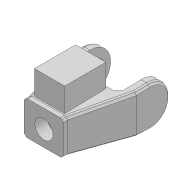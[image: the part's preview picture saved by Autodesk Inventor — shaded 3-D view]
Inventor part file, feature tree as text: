
AUTODESK INVENTOR PART (.ipt)
format: ipt  version: 2018 (Build 220112000, 112)  size: 759,296 bytes
history: native  units: mm
features: sketch x38, extrude x36, projected_geometry x30, chamfer x9, fillet x6, hole x3, mirror x2, plane x1
ambient origin geometry x8: Origin, YZ Plane, XZ Plane, XY Plane, X Axis, Y Axis, Z Axis, Center Point
bodies: Solid1 (feature_tree)
feature tree (125):
  extrude  "Extrusion1"  Depth=45.0mm
  extrude  "Extrusion2"  Depth=2.25mm
  hole  "Hole1"  [1 undecoded]
  hole  "Hole2"  [1 undecoded]
  fillet  "Fillet1"  Radius=14.0mm
  extrude  "Extrusion3"  Depth=18.5mm
  extrude  "Extrusion4"  Depth=10.0mm
  extrude  "Extrusion5"  Depth=2.0mm
  extrude  "Extrusion6"  Depth=2.0mm
  hole  "Hole3"  [1 undecoded]
  extrude  "Extrusion7"  Depth=2.0mm
  extrude  "Extrusion8"  Depth=5.0mm TaperAngle=0.0deg
  extrude  "Extrusion9"  Depth=10.0mm
  extrude  "Extrusion10"  Depth=10.0mm
  extrude  "Extrusion11"  Depth=14.5mm
  extrude  "Extrusion12"  Depth=14.5mm
  extrude  "Extrusion13"  Depth=5.0mm
  extrude  "Extrusion14"  Depth=2.25mm
  extrude  "Extrusion15"  Depth=5.0mm
  extrude  "Extrusion16"  Depth=9.0mm
  extrude  "Extrusion17"  Depth=4.0mm
  chamfer  "Chamfer1"  Distance=1.0mm
  fillet  "Fillet7"  Radius=20.7mm
  fillet  "Fillet8"  Radius=32.0mm
  mirror  "Mirror1"
  extrude  "Extrusion19"  Depth=1.0mm TaperAngle=0.0deg
  extrude  "Extrusion20"  Depth=8.0mm
  extrude  "Extrusion21"  Depth=0.2mm TaperAngle=0.0deg
  extrude  "Extrusion22"  Depth=0.5mm TaperAngle=0.0deg
  sketch  "Sketch29"  dims[d77=12.25mm d78=0.0mm d80=8.0mm]
  extrude  "Extrusion23"  Depth=5.0mm TaperAngle=0.0deg
  extrude  "Extrusion24"  Depth=0.2mm TaperAngle=0.0deg
  plane  "Work Plane1"
  extrude  "Extrusion25"  Depth=2.0mm TaperAngle=45.0deg
  extrude  "Extrusion26"  Depth=0.5mm
  extrude  "Extrusion27"  Depth=8.0mm
  extrude  "Extrusion28"  Depth=3.0mm TaperAngle=0.0deg
  extrude  "Extrusion29"  Depth=33.0mm
  extrude  "Extrusion30"  Depth=56.0mm
  extrude  "Extrusion31"  Depth=25.0mm TaperAngle=0.0deg
  chamfer  "Chamfer2"  Distance=6.0mm
  chamfer  "Chamfer3"  Distance=6.0mm
  chamfer  "Chamfer4"  Distance=4.5mm
  chamfer  "Chamfer5"  Distance=4.5mm
  chamfer  "Chamfer6"  Distance=40.0mm
  fillet  "Fillet9"  Radius=28.0mm
  extrude  "Extrusion34"  Depth=10.0mm
  chamfer  "Chamfer7"  Distance=12.0mm
  chamfer  "Chamfer8"  Distance=40.0mm
  chamfer  "Chamfer9"  Distance=40.0mm
  extrude  "Extrusion35"  Depth=10.0mm
  fillet  "Fillet14"  Radius=1.8mm
  fillet  "Fillet15"  Radius=20.5mm
  sketch  "Sketch47"  dims[d138=2.5mm d139=56.0mm]
  sketch  "Sketch48"  dims[d140=25.0mm d141=0.0mm d142=25.0mm d143=0.0mm d144=6.0mm d145=0.0mm d146=6.0mm d147=0.0mm]
  sketch  "Sketch49"  dims[d149=42.0mm]
  extrude  "Extrusion36"  Depth=10.0mm TaperAngle=0.0deg
  mirror  "Mirror2"
  extrude  "Extrusion37"  Depth=2.0mm TaperAngle=45.0deg
  extrude  "Extrusion38"  Depth=2.0mm TaperAngle=45.0deg
  extrude  "Extrusion39"  Depth=10.0mm TaperAngle=45.0deg
  sketch  "Sketch1"  dims[d0=24.5mm d1=45.0mm]
  sketch  "Sketch2"  dims[d2=1.95mm d3=0.0mm d4=2.25mm]
  projected_geometry  "Projected Loop1"
  sketch  "Sketch3"  dims[d5=20.0mm d6=2.25mm]
  projected_geometry  "Projected Loop2"
  sketch  "Sketch4"  dims[d7=5.25mm d8=5.25mm d9=14.0mm]
  projected_geometry  "Projected Loop3"
  sketch  "Sketch5"  dims[d10=5.25mm d11=18.5mm]
  projected_geometry  "Projected Loop4"
  sketch  "Sketch6"  dims[d12=10.0mm d13=0.0mm d14=20.5mm]
  projected_geometry  "Projected Loop5"
  sketch  "Sketch7"  dims[d15=2.0mm d16=2.195mm]
  projected_geometry  "Projected Loop6"
  sketch  "Sketch8"  dims[d17=2.0mm]
  projected_geometry  "Projected Loop7"
  sketch  "Sketch9"  dims[d18=2.4mm d19=6.0mm d20=4.4mm d21=2.0mm d22=90.0deg d23=8.0mm d24=20.594885mm d25=20.5mm]
  projected_geometry  "Projected Loop8"
  projected_geometry  "Projected Loop9"
  sketch  "Sketch10"  dims[d26=26.65mm d27=2.0mm]
  projected_geometry  "Projected Loop10"
  projected_geometry  "Projected Loop11"
  sketch  "Sketch11"  dims[d28=2.0mm]
  projected_geometry  "Projected Loop12"
  sketch  "Sketch12"  dims[d29=2.4mm d30=6.0mm d31=4.4mm d32=2.0mm d33=90.0deg d34=8.0mm d35=20.594885mm d36=0.5mm]
  sketch  "Sketch13"  dims[d37=18.0mm d38=5.0mm d39=0.0mm]
  sketch  "Sketch14"  dims[d41=10.0mm d42=0.0mm d43=24.5mm]
  projected_geometry  "Projected Loop13"
  sketch  "Sketch15"  dims[d44=1.15mm d45=0.0mm d46=10.0mm]
  sketch  "Sketch16"  dims[d47=21.0mm d48=14.5mm]
  projected_geometry  "Projected Loop14"
  sketch  "Sketch17"  dims[d49=20.0mm d50=14.5mm]
  projected_geometry  "Projected Loop15"
  sketch  "Sketch18"  dims[d51=24.5mm d52=5.0mm]
  projected_geometry  "Projected Loop16"
  sketch  "Sketch19"  dims[d53=5.0mm d54=2.25mm]
  projected_geometry  "Projected Loop17"
  sketch  "Sketch20"  dims[d55=2.25mm d56=5.0mm]
  projected_geometry  "Projected Loop18"
  sketch  "Sketch25"  dims[d57=5.0mm d58=9.0mm]
  projected_geometry  "Projected Loop22"
  sketch  "Sketch26"  dims[d59=14.75mm d60=4.0mm d61=1.0mm d62=0.0mm d63=20.7mm]
  sketch  "Sketch27"  dims[d64=2.4mm d65=6.0mm d66=4.4mm d67=2.0mm d68=90.0deg d69=8.0mm d70=20.594885mm d72=32.0mm]
  projected_geometry  "Projected Loop23"
  sketch  "Sketch28"  dims[d73=5.0mm d74=0.0mm d75=1.0mm d76=0.0mm]
  projected_geometry  "Projected Loop24"
  sketch  "Sketch31"  dims[d81=4.5mm d82=0.0mm d84=0.2mm d85=0.0mm]
  projected_geometry  "Projected Loop25"
  sketch  "Sketch32"  dims[d86=21.0mm d87=0.5mm d88=0.0mm]
  projected_geometry  "Projected Loop26"
  sketch  "Sketch33"  dims[d91=8.0mm d92=0.0mm d93=5.0mm d94=0.0mm]
  sketch  "Sketch34"  dims[d95=5.0mm d96=0.0mm d98=0.2mm d99=0.0mm]
  sketch  "Sketch35"  dims[d100=0.2mm d101=0.0mm d102=2.5mm d103=2.0mm d104=45.0deg]
  projected_geometry  "Projected Loop27"
  sketch  "Sketch36"  dims[d105=1.5mm d114=0.5mm]
  sketch  "Sketch37"  dims[d128=4.0mm d129=0.0mm d130=8.0mm]
  sketch  "Sketch41"  dims[d131=3.0mm d132=0.0mm d133=3.0mm d134=0.0mm]
  sketch  "Sketch44"  dims[d135=25.0mm d136=0.0mm d137=33.0mm]
  projected_geometry  "Projected Loop31"
  projected_geometry  "Projected Loop34"
  sketch  "Sketch50"  dims[d150=4.5mm d151=4.5mm d152=4.5mm d153=40.0mm d154=0.0mm d155=28.0mm d156=12.0mm d157=12.0mm d158=40.0mm d159=0.0mm d160=40.0mm d161=0.0mm d162=20.5mm d163=1.8mm d164=0.0mm d165=20.5mm d166=3.3mm d167=0.0mm d168=2.0mm d169=2.0mm d170=45.0deg d179=1.2mm d180=2.0mm d181=45.0deg d188=3.0mm d189=15.0mm d190=45.0deg d191=3.0mm d192=15.0mm d193=45.0deg d194=3.0mm d195=15.0mm d196=45.0deg d197=2.0mm d198=12.0mm d199=2.0mm d200=15.0mm d201=20.0mm d202=0.0mm d203=2.0mm d204=15.0mm d205=45.0deg d232=2.0mm d233=15.0mm d234=45.0deg d235=2.0mm d236=15.0mm d237=45.0deg d240=3.9mm d241=3.9mm d242=3.5mm d243=0.0mm d269=2.0mm d270=2.0mm d274=2.0mm d275=15.0mm d276=10.0mm d277=0.0mm d278=45.0mm d279=0.0mm d280=45.0mm d281=0.0mm d282=10.0mm d283=0.0mm]
  projected_geometry  "Projected Loop35"
  projected_geometry  "Project Cut Edges1"
  projected_geometry  "Project Cut Edges2"
  projected_geometry  "Project Cut Edges4"
note: 3 required parameter values undecoded (feature->parameter linkage not recoverable at this tier; creation-order binding heuristic only, values carry confidence <= 0.55)
